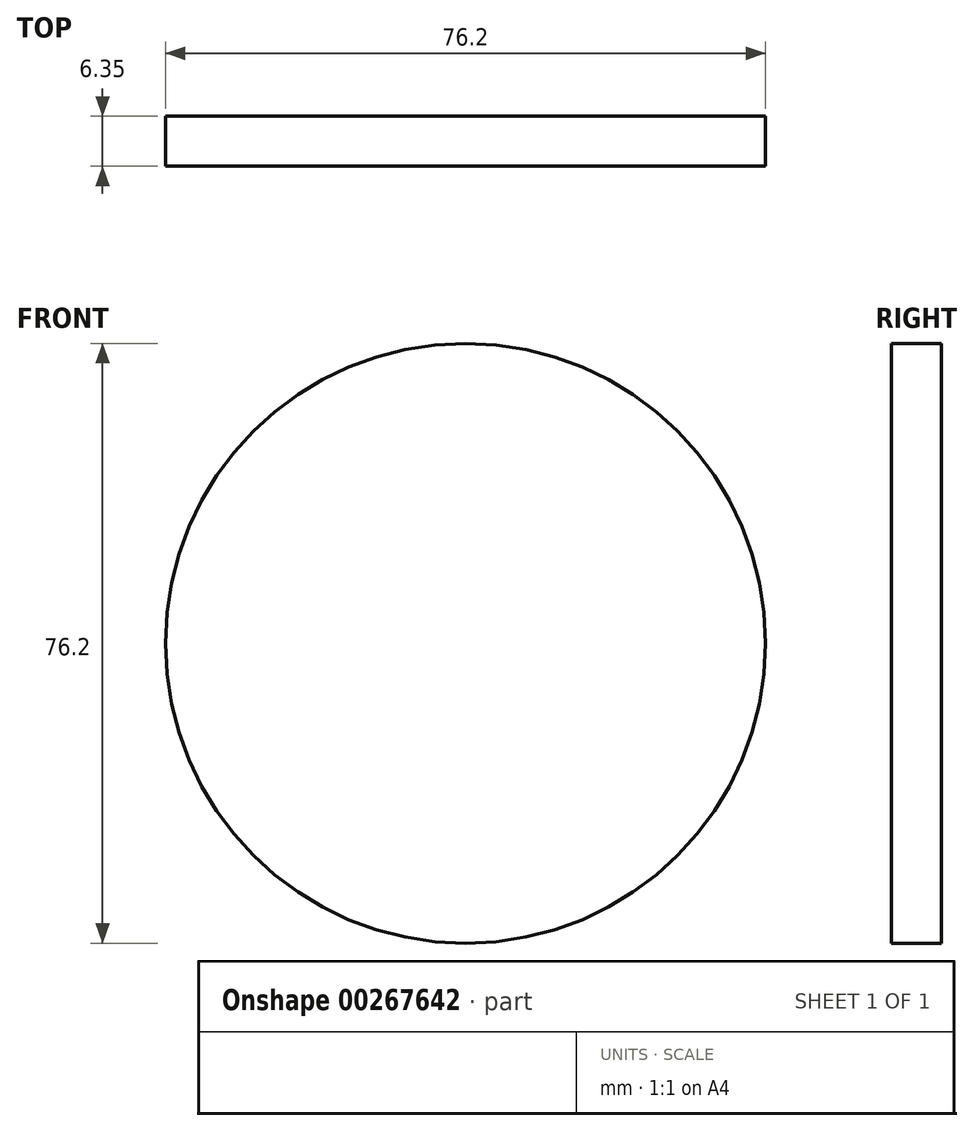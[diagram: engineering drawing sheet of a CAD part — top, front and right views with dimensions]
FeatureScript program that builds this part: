
annotation { "Feature Type Name" : "Feature", "Feature Type Description" : "" }
export const myFeature = defineFeature(function(context is Context, id is Id, definition is map)
    precondition{}
    {
        {
            var Q0;
            Q0=qCreatedBy(makeId("Front.planeOp"),FACE);
            var sketch = newSketch(context, id + "F0", { "sketchPlane" : qUnion([Q0])});
            skCircle(sketch, "E0", {"center": v(0, 0) * mm, "radius": 38.1 * mm});
            skSolve(sketch);
        }
        {
            var Q0;
            Q0=makeQuery(id+"F0.imprint","IMPRINT",FACE,{"disambiguationData":[TD([[makeQuery(id+"F0.imprint","IMPRINT",EDGE,{"derivedFrom":sQuery(id+"F0.wireOp",EDGE,"E0")}),1.0]])]});
            extrude(context, id + "F1", {"entities" : qUnion([Q0]), "depth" : 6.35 * mm});
        }
    });
